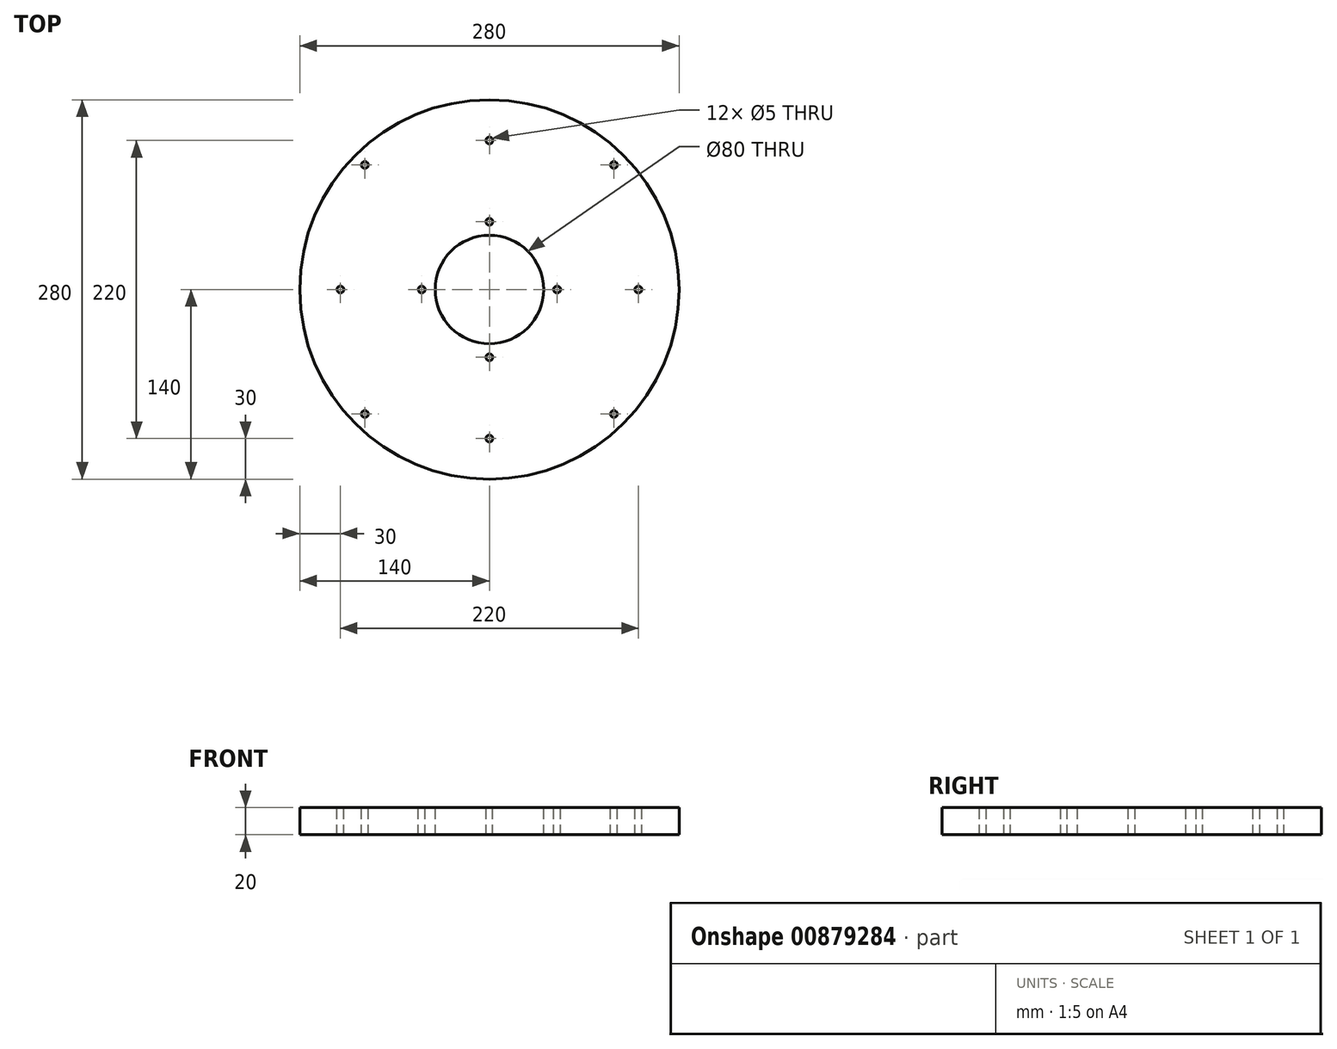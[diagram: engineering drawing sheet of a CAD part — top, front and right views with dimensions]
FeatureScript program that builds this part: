
annotation { "Feature Type Name" : "Feature", "Feature Type Description" : "" }
export const myFeature = defineFeature(function(context is Context, id is Id, definition is map)
    precondition{}
    {
        {
            var Q0;
            Q0=qCreatedBy(makeId("Top.planeOp"),FACE);
            var sketch = newSketch(context, id + "F0", { "sketchPlane" : qUnion([Q0])});
            skCircle(sketch, "E0", {"center": v(0, 0) * mm, "radius": 140 * mm});
            skSolve(sketch);
        }
        {
            var Q0;
            Q0 = qSketchRegion(id + "F0", true);
            extrude(context, id + "F1", {"entities" : qUnion([Q0]), "depth" : 20 * mm, "offsetDistance" : 25 * mm});
        }
        {
            var Q0;
            Q0=makeQuery(id+"F1.opExtrude","CAP_FACE",FACE,{"disambiguationData":[OSD([sQuery(id+"F0.wireOp",EDGE,"E0")])],"isStart":false});
            var sketch = newSketch(context, id + "F2", { "sketchPlane" : qUnion([Q0])});
            skCircle(sketch, "E1", {"center": v(0, 0) * mm, "radius": 110 * mm});
            skCircle(sketch, "E2", {"center": v(0, 110) * mm, "radius": 2.5 * mm});
            skCircle(sketch, "E3", {"center": v(110, 0) * mm, "radius": 2.5 * mm});
            skCircle(sketch, "E4", {"center": v(0, -110) * mm, "radius": 2.5 * mm});
            skCircle(sketch, "E5", {"center": v(-110, 0) * mm, "radius": 2.5 * mm});
            skSolve(sketch);
        }
        {
            var Q0;
            {var subQ0=sQuery(id+"F2.wireOp",EDGE,"E2");var subQ1=sQuery(id+"F2.wireOp",EDGE,"E1");var subQ2=makeQuery(id+"F2.imprint","INTERSECT",VERTEX,{"disambiguationData":[OD(0.0)],"derivedFrom":[subQ1,subQ0]});Q0=makeQuery(id+"F2.imprint","IMPRINT",FACE,{"disambiguationData":[TD([[makeQuery(id+"F2.imprint","IMPRINT",EDGE,{"disambiguationData":[TD([[subQ2,-1.0]])],"derivedFrom":subQ1}),-1.0]])]});}
            var Q1;
            {var subQ0=sQuery(id+"F2.wireOp",EDGE,"E2");var subQ1=sQuery(id+"F2.wireOp",EDGE,"E1");var subQ2=makeQuery(id+"F2.imprint","INTERSECT",VERTEX,{"disambiguationData":[OD(0.0)],"derivedFrom":[subQ1,subQ0]});Q1=makeQuery(id+"F2.imprint","IMPRINT",FACE,{"disambiguationData":[TD([[makeQuery(id+"F2.imprint","IMPRINT",EDGE,{"disambiguationData":[TD([[subQ2,-1.0]])],"derivedFrom":subQ1}),1.0]])]});}
            var Q2;
            {var subQ0=sQuery(id+"F2.wireOp",EDGE,"E3");var subQ1=sQuery(id+"F2.wireOp",EDGE,"E1");var subQ2=makeQuery(id+"F2.imprint","INTERSECT",VERTEX,{"disambiguationData":[OD(0.0)],"derivedFrom":[subQ1,subQ0]});Q2=makeQuery(id+"F2.imprint","IMPRINT",FACE,{"disambiguationData":[TD([[makeQuery(id+"F2.imprint","IMPRINT",EDGE,{"disambiguationData":[TD([[subQ2,1.0]])],"derivedFrom":subQ1}),-1.0]])]});}
            var Q3;
            {var subQ0=sQuery(id+"F2.wireOp",EDGE,"E3");var subQ1=sQuery(id+"F2.wireOp",EDGE,"E1");var subQ2=makeQuery(id+"F2.imprint","INTERSECT",VERTEX,{"disambiguationData":[OD(0.0)],"derivedFrom":[subQ1,subQ0]});Q3=makeQuery(id+"F2.imprint","IMPRINT",FACE,{"disambiguationData":[TD([[makeQuery(id+"F2.imprint","IMPRINT",EDGE,{"disambiguationData":[TD([[subQ2,1.0]])],"derivedFrom":subQ1}),1.0]])]});}
            var Q4;
            {var subQ0=sQuery(id+"F2.wireOp",EDGE,"E4");var subQ1=sQuery(id+"F2.wireOp",EDGE,"E1");var subQ2=makeQuery(id+"F2.imprint","INTERSECT",VERTEX,{"disambiguationData":[OD(0.0)],"derivedFrom":[subQ1,subQ0]});Q4=makeQuery(id+"F2.imprint","IMPRINT",FACE,{"disambiguationData":[TD([[makeQuery(id+"F2.imprint","IMPRINT",EDGE,{"disambiguationData":[TD([[subQ2,-1.0]])],"derivedFrom":subQ1}),-1.0]])]});}
            var Q5;
            {var subQ0=sQuery(id+"F2.wireOp",EDGE,"E4");var subQ1=sQuery(id+"F2.wireOp",EDGE,"E1");var subQ2=makeQuery(id+"F2.imprint","INTERSECT",VERTEX,{"disambiguationData":[OD(0.0)],"derivedFrom":[subQ1,subQ0]});Q5=makeQuery(id+"F2.imprint","IMPRINT",FACE,{"disambiguationData":[TD([[makeQuery(id+"F2.imprint","IMPRINT",EDGE,{"disambiguationData":[TD([[subQ2,-1.0]])],"derivedFrom":subQ1}),1.0]])]});}
            var Q6;
            {var subQ0=sQuery(id+"F2.wireOp",EDGE,"E5");var subQ1=sQuery(id+"F2.wireOp",EDGE,"E1");var subQ2=makeQuery(id+"F2.imprint","INTERSECT",VERTEX,{"disambiguationData":[OD(0.0)],"derivedFrom":[subQ1,subQ0]});Q6=makeQuery(id+"F2.imprint","IMPRINT",FACE,{"disambiguationData":[TD([[makeQuery(id+"F2.imprint","IMPRINT",EDGE,{"disambiguationData":[TD([[subQ2,-1.0]])],"derivedFrom":subQ1}),1.0]])]});}
            var Q7;
            {var subQ0=sQuery(id+"F2.wireOp",EDGE,"E5");var subQ1=sQuery(id+"F2.wireOp",EDGE,"E1");var subQ2=makeQuery(id+"F2.imprint","INTERSECT",VERTEX,{"disambiguationData":[OD(0.0)],"derivedFrom":[subQ1,subQ0]});Q7=makeQuery(id+"F2.imprint","IMPRINT",FACE,{"disambiguationData":[TD([[makeQuery(id+"F2.imprint","IMPRINT",EDGE,{"disambiguationData":[TD([[subQ2,-1.0]])],"derivedFrom":subQ1}),-1.0]])]});}
            extrude(context, id + "F3", {"entities" : qUnion([Q0, Q1, Q2, Q3, Q4, Q5, Q6, Q7]), "operationType" : NewBodyOperationType.REMOVE, "endBound" : BoundingType.THROUGH_ALL, "oppositeDirection" : true, "depth" : 25 * mm, "offsetDistance" : 25 * mm});
        }
        {
            var Q0;
            Q0=makeQuery(id+"F1.opExtrude","CAP_FACE",FACE,{"disambiguationData":[OSD([sQuery(id+"F0.wireOp",EDGE,"E0")])],"isStart":false});
            var sketch = newSketch(context, id + "F4", { "sketchPlane" : qUnion([Q0])});
            skCircle(sketch, "E6", {"center": v(0, 0) * mm, "radius": 130 * mm});
            skLineSegment(sketch, "E7", {"start": v(-91.92, 91.92) * mm, "end": v(0, 0) * mm});
            skCircle(sketch, "E8", {"center": v(-91.92, 91.92) * mm, "radius": 2.5 * mm});
            skLineSegment(sketch, "E9", {"start": v(0, 0) * mm, "end": v(91.92, -91.92) * mm});
            skCircle(sketch, "E10", {"center": v(91.92, -91.92) * mm, "radius": 2.5 * mm});
            skLineSegment(sketch, "E11", {"start": v(0, 0) * mm, "end": v(91.92, 91.92) * mm});
            skCircle(sketch, "E12", {"center": v(91.92, 91.92) * mm, "radius": 2.5 * mm});
            skLineSegment(sketch, "E13", {"start": v(0, 0) * mm, "end": v(-91.92, -91.92) * mm});
            skCircle(sketch, "E14", {"center": v(-91.92, -91.92) * mm, "radius": 2.5 * mm});
            skSolve(sketch);
        }
        {
            var Q0;
            {var subQ0=sQuery(id+"F4.wireOp",EDGE,"E7");var subQ1=sQuery(id+"F4.wireOp",EDGE,"E6");var subQ2=makeQuery(id+"F4.imprint","INTERSECT",VERTEX,{"derivedFrom":[subQ1,subQ0]});Q0=makeQuery(id+"F4.imprint","IMPRINT",FACE,{"disambiguationData":[TD([[makeQuery(id+"F4.imprint","IMPRINT",EDGE,{"disambiguationData":[TD([[subQ2,1.0]])],"derivedFrom":subQ1}),1.0]])]});}
            var Q1;
            {var subQ0=sQuery(id+"F4.wireOp",EDGE,"E7");var subQ1=sQuery(id+"F4.wireOp",EDGE,"E6");var subQ2=makeQuery(id+"F4.imprint","INTERSECT",VERTEX,{"derivedFrom":[subQ1,subQ0]});Q1=makeQuery(id+"F4.imprint","IMPRINT",FACE,{"disambiguationData":[TD([[makeQuery(id+"F4.imprint","IMPRINT",EDGE,{"disambiguationData":[TD([[subQ2,-1.0]])],"derivedFrom":subQ1}),1.0]])]});}
            var Q2;
            {var subQ0=sQuery(id+"F4.wireOp",EDGE,"E6");var subQ1=makeQuery(id+"F4.imprint","INTERSECT",VERTEX,{"derivedFrom":[subQ0,sQuery(id+"F4.wireOp",EDGE,"E7")]});Q2=makeQuery(id+"F4.imprint","IMPRINT",FACE,{"disambiguationData":[TD([[makeQuery(id+"F4.imprint","IMPRINT",EDGE,{"disambiguationData":[TD([[subQ1,1.0]])],"derivedFrom":subQ0}),-1.0]])]});}
            var Q3;
            {var subQ0=sQuery(id+"F4.wireOp",EDGE,"E6");var subQ1=makeQuery(id+"F4.imprint","INTERSECT",VERTEX,{"derivedFrom":[subQ0,sQuery(id+"F4.wireOp",EDGE,"E11")]});Q3=makeQuery(id+"F4.imprint","IMPRINT",FACE,{"disambiguationData":[TD([[makeQuery(id+"F4.imprint","IMPRINT",EDGE,{"disambiguationData":[TD([[subQ1,1.0]])],"derivedFrom":subQ0}),-1.0]])]});}
            var Q4;
            {var subQ0=sQuery(id+"F4.wireOp",EDGE,"E11");var subQ1=sQuery(id+"F4.wireOp",EDGE,"E6");var subQ2=makeQuery(id+"F4.imprint","INTERSECT",VERTEX,{"derivedFrom":[subQ1,subQ0]});Q4=makeQuery(id+"F4.imprint","IMPRINT",FACE,{"disambiguationData":[TD([[makeQuery(id+"F4.imprint","IMPRINT",EDGE,{"disambiguationData":[TD([[subQ2,1.0]])],"derivedFrom":subQ1}),1.0]])]});}
            var Q5;
            {var subQ0=sQuery(id+"F4.wireOp",EDGE,"E11");var subQ1=sQuery(id+"F4.wireOp",EDGE,"E6");var subQ2=makeQuery(id+"F4.imprint","INTERSECT",VERTEX,{"derivedFrom":[subQ1,subQ0]});Q5=makeQuery(id+"F4.imprint","IMPRINT",FACE,{"disambiguationData":[TD([[makeQuery(id+"F4.imprint","IMPRINT",EDGE,{"disambiguationData":[TD([[subQ2,-1.0]])],"derivedFrom":subQ1}),1.0]])]});}
            var Q6;
            {var subQ0=sQuery(id+"F4.wireOp",EDGE,"E6");var subQ1=makeQuery(id+"F4.imprint","INTERSECT",VERTEX,{"derivedFrom":[subQ0,sQuery(id+"F4.wireOp",EDGE,"E9")]});Q6=makeQuery(id+"F4.imprint","IMPRINT",FACE,{"disambiguationData":[TD([[makeQuery(id+"F4.imprint","IMPRINT",EDGE,{"disambiguationData":[TD([[subQ1,1.0]])],"derivedFrom":subQ0}),-1.0]])]});}
            var Q7;
            {var subQ0=sQuery(id+"F4.wireOp",EDGE,"E9");var subQ1=sQuery(id+"F4.wireOp",EDGE,"E6");var subQ2=makeQuery(id+"F4.imprint","INTERSECT",VERTEX,{"derivedFrom":[subQ1,subQ0]});Q7=makeQuery(id+"F4.imprint","IMPRINT",FACE,{"disambiguationData":[TD([[makeQuery(id+"F4.imprint","IMPRINT",EDGE,{"disambiguationData":[TD([[subQ2,-1.0]])],"derivedFrom":subQ1}),1.0]])]});}
            var Q8;
            {var subQ0=sQuery(id+"F4.wireOp",EDGE,"E9");var subQ1=sQuery(id+"F4.wireOp",EDGE,"E6");var subQ2=makeQuery(id+"F4.imprint","INTERSECT",VERTEX,{"derivedFrom":[subQ1,subQ0]});Q8=makeQuery(id+"F4.imprint","IMPRINT",FACE,{"disambiguationData":[TD([[makeQuery(id+"F4.imprint","IMPRINT",EDGE,{"disambiguationData":[TD([[subQ2,1.0]])],"derivedFrom":subQ1}),1.0]])]});}
            var Q9;
            {var subQ0=sQuery(id+"F4.wireOp",EDGE,"E13");var subQ1=sQuery(id+"F4.wireOp",EDGE,"E6");var subQ2=makeQuery(id+"F4.imprint","INTERSECT",VERTEX,{"derivedFrom":[subQ1,subQ0]});Q9=makeQuery(id+"F4.imprint","IMPRINT",FACE,{"disambiguationData":[TD([[makeQuery(id+"F4.imprint","IMPRINT",EDGE,{"disambiguationData":[TD([[subQ2,-1.0]])],"derivedFrom":subQ1}),1.0]])]});}
            var Q10;
            {var subQ0=sQuery(id+"F4.wireOp",EDGE,"E6");var subQ1=makeQuery(id+"F4.imprint","INTERSECT",VERTEX,{"derivedFrom":[subQ0,sQuery(id+"F4.wireOp",EDGE,"E13")]});Q10=makeQuery(id+"F4.imprint","IMPRINT",FACE,{"disambiguationData":[TD([[makeQuery(id+"F4.imprint","IMPRINT",EDGE,{"disambiguationData":[TD([[subQ1,1.0]])],"derivedFrom":subQ0}),-1.0]])]});}
            var Q11;
            {var subQ0=sQuery(id+"F4.wireOp",EDGE,"E13");var subQ1=sQuery(id+"F4.wireOp",EDGE,"E6");var subQ2=makeQuery(id+"F4.imprint","INTERSECT",VERTEX,{"derivedFrom":[subQ1,subQ0]});Q11=makeQuery(id+"F4.imprint","IMPRINT",FACE,{"disambiguationData":[TD([[makeQuery(id+"F4.imprint","IMPRINT",EDGE,{"disambiguationData":[TD([[subQ2,1.0]])],"derivedFrom":subQ1}),1.0]])]});}
            extrude(context, id + "F5", {"entities" : qUnion([Q0, Q1, Q2, Q3, Q4, Q5, Q6, Q7, Q8, Q9, Q10, Q11]), "operationType" : NewBodyOperationType.REMOVE, "oppositeDirection" : true, "depth" : 25 * mm, "offsetDistance" : 25 * mm});
        }
        {
            var Q0;
            Q0=makeQuery(id+"F1.opExtrude","CAP_FACE",FACE,{"disambiguationData":[OSD([sQuery(id+"F0.wireOp",EDGE,"E0")])],"isStart":false});
            var sketch = newSketch(context, id + "F6", { "sketchPlane" : qUnion([Q0])});
            skCircle(sketch, "E15", {"center": v(0, 0) * mm, "radius": 40 * mm});
            skSolve(sketch);
        }
        {
            var Q0;
            Q0=makeQuery(id+"F6.imprint","IMPRINT",FACE,{"disambiguationData":[TD([[makeQuery(id+"F6.imprint","IMPRINT",EDGE,{"derivedFrom":sQuery(id+"F6.wireOp",EDGE,"E15")}),1.0]])]});
            extrude(context, id + "F7", {"entities" : qUnion([Q0]), "operationType" : NewBodyOperationType.REMOVE, "oppositeDirection" : true, "depth" : 25 * mm, "offsetDistance" : 25 * mm});
        }
        {
            var Q0;
            Q0=makeQuery(id+"F1.opExtrude","CAP_FACE",FACE,{"disambiguationData":[OSD([sQuery(id+"F0.wireOp",EDGE,"E0")])],"isStart":false});
            var sketch = newSketch(context, id + "F8", { "sketchPlane" : qUnion([Q0])});
            skCircle(sketch, "E16", {"center": v(0, 0) * mm, "radius": 50 * mm});
            skCircle(sketch, "E17", {"center": v(0, 50) * mm, "radius": 2.5 * mm});
            skCircle(sketch, "E18", {"center": v(0, -50) * mm, "radius": 2.5 * mm});
            skCircle(sketch, "E19", {"center": v(-50, 0) * mm, "radius": 2.5 * mm});
            skCircle(sketch, "E20", {"center": v(50, 0) * mm, "radius": 2.5 * mm});
            skSolve(sketch);
        }
        {
            var Q0;
            {var subQ0=sQuery(id+"F8.wireOp",EDGE,"E17");var subQ1=sQuery(id+"F8.wireOp",EDGE,"E16");var subQ2=makeQuery(id+"F8.imprint","INTERSECT",VERTEX,{"disambiguationData":[OD(0.0)],"derivedFrom":[subQ1,subQ0]});Q0=makeQuery(id+"F8.imprint","IMPRINT",FACE,{"disambiguationData":[TD([[makeQuery(id+"F8.imprint","IMPRINT",EDGE,{"disambiguationData":[TD([[subQ2,-1.0]])],"derivedFrom":subQ1}),-1.0]])]});}
            var Q1;
            {var subQ0=sQuery(id+"F8.wireOp",EDGE,"E17");var subQ1=sQuery(id+"F8.wireOp",EDGE,"E16");var subQ2=makeQuery(id+"F8.imprint","INTERSECT",VERTEX,{"disambiguationData":[OD(0.0)],"derivedFrom":[subQ1,subQ0]});Q1=makeQuery(id+"F8.imprint","IMPRINT",FACE,{"disambiguationData":[TD([[makeQuery(id+"F8.imprint","IMPRINT",EDGE,{"disambiguationData":[TD([[subQ2,-1.0]])],"derivedFrom":subQ1}),1.0]])]});}
            var Q2;
            {var subQ0=sQuery(id+"F8.wireOp",EDGE,"E19");var subQ1=sQuery(id+"F8.wireOp",EDGE,"E16");var subQ2=makeQuery(id+"F8.imprint","INTERSECT",VERTEX,{"disambiguationData":[OD(0.0)],"derivedFrom":[subQ1,subQ0]});Q2=makeQuery(id+"F8.imprint","IMPRINT",FACE,{"disambiguationData":[TD([[makeQuery(id+"F8.imprint","IMPRINT",EDGE,{"disambiguationData":[TD([[subQ2,-1.0]])],"derivedFrom":subQ1}),1.0]])]});}
            var Q3;
            {var subQ0=sQuery(id+"F8.wireOp",EDGE,"E19");var subQ1=sQuery(id+"F8.wireOp",EDGE,"E16");var subQ2=makeQuery(id+"F8.imprint","INTERSECT",VERTEX,{"disambiguationData":[OD(0.0)],"derivedFrom":[subQ1,subQ0]});Q3=makeQuery(id+"F8.imprint","IMPRINT",FACE,{"disambiguationData":[TD([[makeQuery(id+"F8.imprint","IMPRINT",EDGE,{"disambiguationData":[TD([[subQ2,-1.0]])],"derivedFrom":subQ1}),-1.0]])]});}
            var Q4;
            {var subQ0=sQuery(id+"F8.wireOp",EDGE,"E18");var subQ1=sQuery(id+"F8.wireOp",EDGE,"E16");var subQ2=makeQuery(id+"F8.imprint","INTERSECT",VERTEX,{"disambiguationData":[OD(0.0)],"derivedFrom":[subQ1,subQ0]});Q4=makeQuery(id+"F8.imprint","IMPRINT",FACE,{"disambiguationData":[TD([[makeQuery(id+"F8.imprint","IMPRINT",EDGE,{"disambiguationData":[TD([[subQ2,-1.0]])],"derivedFrom":subQ1}),-1.0]])]});}
            var Q5;
            {var subQ0=sQuery(id+"F8.wireOp",EDGE,"E18");var subQ1=sQuery(id+"F8.wireOp",EDGE,"E16");var subQ2=makeQuery(id+"F8.imprint","INTERSECT",VERTEX,{"disambiguationData":[OD(0.0)],"derivedFrom":[subQ1,subQ0]});Q5=makeQuery(id+"F8.imprint","IMPRINT",FACE,{"disambiguationData":[TD([[makeQuery(id+"F8.imprint","IMPRINT",EDGE,{"disambiguationData":[TD([[subQ2,-1.0]])],"derivedFrom":subQ1}),1.0]])]});}
            var Q6;
            {var subQ0=sQuery(id+"F8.wireOp",EDGE,"E20");var subQ1=sQuery(id+"F8.wireOp",EDGE,"E16");var subQ2=makeQuery(id+"F8.imprint","INTERSECT",VERTEX,{"disambiguationData":[OD(0.0)],"derivedFrom":[subQ1,subQ0]});Q6=makeQuery(id+"F8.imprint","IMPRINT",FACE,{"disambiguationData":[TD([[makeQuery(id+"F8.imprint","IMPRINT",EDGE,{"disambiguationData":[TD([[subQ2,1.0]])],"derivedFrom":subQ1}),-1.0]])]});}
            var Q7;
            {var subQ0=sQuery(id+"F8.wireOp",EDGE,"E20");var subQ1=sQuery(id+"F8.wireOp",EDGE,"E16");var subQ2=makeQuery(id+"F8.imprint","INTERSECT",VERTEX,{"disambiguationData":[OD(0.0)],"derivedFrom":[subQ1,subQ0]});Q7=makeQuery(id+"F8.imprint","IMPRINT",FACE,{"disambiguationData":[TD([[makeQuery(id+"F8.imprint","IMPRINT",EDGE,{"disambiguationData":[TD([[subQ2,1.0]])],"derivedFrom":subQ1}),1.0]])]});}
            extrude(context, id + "F9", {"entities" : qUnion([Q0, Q1, Q2, Q3, Q4, Q5, Q6, Q7]), "operationType" : NewBodyOperationType.REMOVE, "oppositeDirection" : true, "depth" : 25 * mm, "offsetDistance" : 25 * mm});
        }
    });
